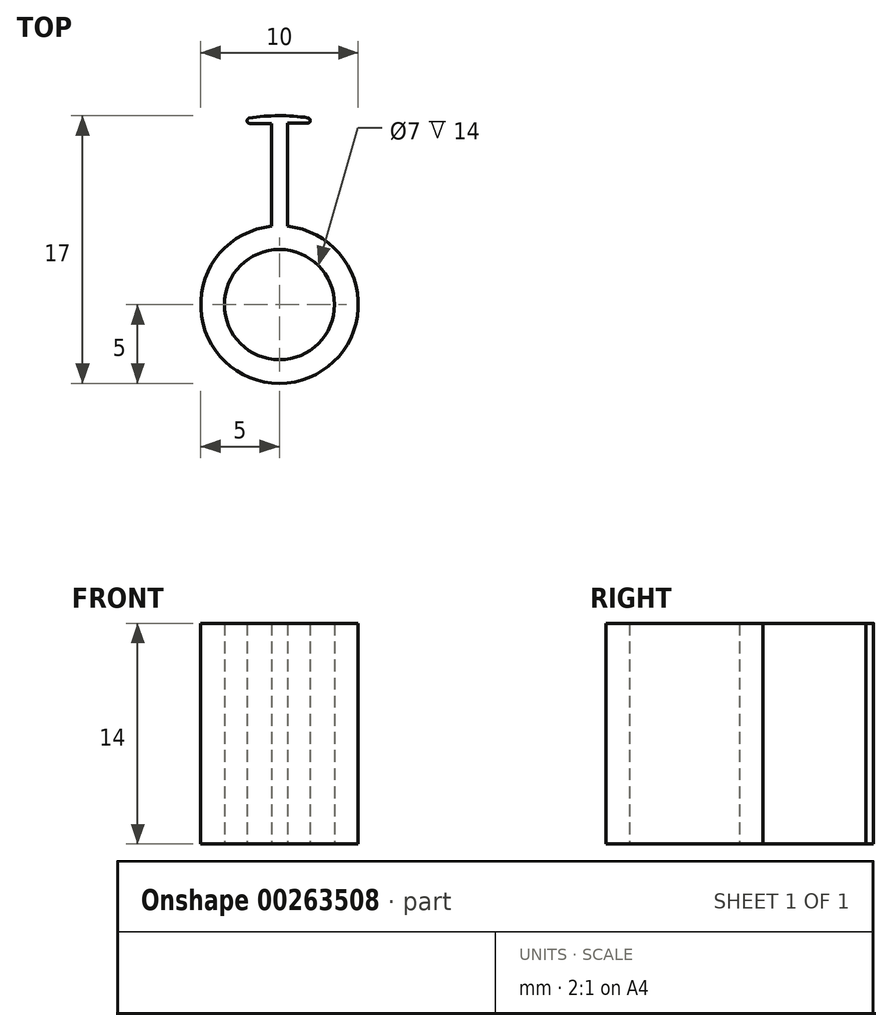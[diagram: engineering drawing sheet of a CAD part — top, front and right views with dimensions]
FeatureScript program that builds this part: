
annotation { "Feature Type Name" : "Feature", "Feature Type Description" : "" }
export const myFeature = defineFeature(function(context is Context, id is Id, definition is map)
    precondition{}
    {
        {
            var Q0;
            Q0=qCreatedBy(makeId("Top.planeOp"),FACE);
            var sketch = newSketch(context, id + "F0", { "sketchPlane" : qUnion([Q0])});
            skCircle(sketch, "E0", {"center": v(0, 0) * mm, "radius": 3.5 * mm});
            skCircle(sketch, "E1", {"center": v(0, 0) * mm, "radius": 5 * mm});
            skSolve(sketch);
        }
        {
            var Q0;
            Q0=makeQuery(id+"F0.imprint","IMPRINT",FACE,{"disambiguationData":[TD([[makeQuery(id+"F0.imprint","IMPRINT",EDGE,{"derivedFrom":sQuery(id+"F0.wireOp",EDGE,"E0")}),-1.0]])]});
            extrude(context, id + "F1", {"entities" : qUnion([Q0]), "depth" : 11 * mm});
        }
        {
            var Q0;
            Q0=makeQuery(id+"F1.opExtrude","CAP_FACE",FACE,{"disambiguationData":[OSD([sQuery(id+"F0.wireOp",EDGE,"E0"),sQuery(id+"F0.wireOp",EDGE,"E1")])],"isStart":true});
            var sketch = newSketch(context, id + "F2", { "sketchPlane" : qUnion([Q0])});
            skLineSegment(sketch, "E2.bottom", {"start": v(-0.5, 0) * mm, "end": v(0.5, 0) * mm});
            skLineSegment(sketch, "E2.top", {"start": v(-0.5, -12) * mm, "end": v(0.5, -12) * mm});
            skLineSegment(sketch, "E2.left", {"start": v(-0.5, 0) * mm, "end": v(-0.5, -12) * mm});
            skLineSegment(sketch, "E2.right", {"start": v(0.5, 0) * mm, "end": v(0.5, -12) * mm});
            skArc(sketch, "E3", {"start": v(0, -12) * mm, "mid": v(0.98, -11.96) * mm, "end": v(1.94, -11.84) * mm});
            skArc(sketch, "E4", {"start": v(0, -12) * mm, "mid": v(-1.03, -11.96) * mm, "end": v(-2.05, -11.82) * mm});
            skLineSegment(sketch, "E5", {"start": v(-2.05, -11.82) * mm, "end": v(-2.05, -11.51) * mm});
            skLineSegment(sketch, "E6", {"start": v(-2.05, -11.51) * mm, "end": v(-0.5, -11.51) * mm});
            skLineSegment(sketch, "E7", {"start": v(1.94, -11.84) * mm, "end": v(1.94, -11.53) * mm});
            skLineSegment(sketch, "E8", {"start": v(1.94, -11.53) * mm, "end": v(0.5, -11.53) * mm});
            skSolve(sketch);
        }
        {
            var Q0;
            {var subQ4=sQuery(id+"F2.wireOp",EDGE,"E5");Q0=makeQuery(id+"F2.imprint","IMPRINT",FACE,{"disambiguationData":[TD([[makeQuery(id+"F2.imprint","IMPRINT",EDGE,{"derivedFrom":subQ4}),-1.0]])]});}
            var Q1;
            {var subQ4=sQuery(id+"F2.wireOp",EDGE,"E7");Q1=makeQuery(id+"F2.imprint","IMPRINT",FACE,{"disambiguationData":[TD([[makeQuery(id+"F2.imprint","IMPRINT",EDGE,{"derivedFrom":subQ4}),1.0]])]});}
            var Q2;
            {var subQ4=sQuery(id+"F2.wireOp",EDGE,"E2.left");var subQ5=makeQuery(id+"F2.imprint","INTERSECT",VERTEX,{"derivedFrom":[subQ4,sQuery(id+"F2.wireOp",EDGE,"E6")]});Q2=makeQuery(id+"F2.imprint","IMPRINT",FACE,{"disambiguationData":[TD([[makeQuery(id+"F2.imprint","IMPRINT",EDGE,{"disambiguationData":[TD([[subQ5,1.0]])],"derivedFrom":subQ4}),1.0]])]});}
            extrude(context, id + "F3", {"entities" : qUnion([Q0, Q1, Q2]), "operationType" : NewBodyOperationType.ADD, "oppositeDirection" : true, "depth" : 11 * mm});
        }
        {
            var Q0;
            Q0=makeQuery(id+"F3.opExtrude","SWEPT_EDGE",EDGE,{"disambiguationData":[OSD([sQuery(id+"F2.wireOp",EDGE,"E5"),sQuery(id+"F2.wireOp",EDGE,"E6")])]});
            var Q1;
            Q1=makeQuery(id+"F3.opExtrude","SWEPT_EDGE",EDGE,{"disambiguationData":[OSD([sQuery(id+"F2.wireOp",EDGE,"E4"),sQuery(id+"F2.wireOp",EDGE,"E5")])]});
            var Q2;
            Q2=makeQuery(id+"F3.opExtrude","SWEPT_EDGE",EDGE,{"disambiguationData":[OSD([sQuery(id+"F2.wireOp",EDGE,"E3"),sQuery(id+"F2.wireOp",EDGE,"E7")])]});
            var Q3;
            Q3=makeQuery(id+"F3.opExtrude","SWEPT_EDGE",EDGE,{"disambiguationData":[OSD([sQuery(id+"F2.wireOp",EDGE,"E7"),sQuery(id+"F2.wireOp",EDGE,"E8")])]});
            fillet(context, id + "F4", {"entities" : qUnion([Q0, Q1, Q2, Q3]), "radius" : 0.15 * mm, "tangentPropagation" : true, "allowEdgeOverflow" : false});
        }
        {
            var Q0;
            Q0=qCreatedBy(makeId("Right.planeOp"),FACE);
            var sketch = newSketch(context, id + "F5", { "sketchPlane" : qUnion([Q0])});
            skLineSegment(sketch, "E9", {"start": v(0, 0) * mm, "end": v(0, 33.12) * mm});
            skSolve(sketch);
        }
        {
            var Q0;
            {var subQ0=sQuery(id+"F2.wireOp",EDGE,"E8");var subQ1=sQuery(id+"F2.wireOp",EDGE,"E7");var subQ2=sQuery(id+"F2.wireOp",EDGE,"E6");var subQ3=sQuery(id+"F2.wireOp",EDGE,"E5");var subQ4=sQuery(id+"F2.wireOp",EDGE,"E4");var subQ5=sQuery(id+"F2.wireOp",EDGE,"E3");var subQ6=sQuery(id+"F2.wireOp",EDGE,"E2.right");var subQ7=sQuery(id+"F2.wireOp",EDGE,"E2.left");var subQ8=sQuery(id+"F0.wireOp",EDGE,"E1");Q0=makeQuery(id+"FQCFKPcWUteTYy7_1.13.F3.boolean.opBoolean","MERGE",FACE,{"derivedFrom":[makeQuery(id+"FQCFKPcWUteTYy7_1.12.F3.boolean.opBoolean","MERGE",FACE,{"derivedFrom":[makeQuery(id+"FQCFKPcWUteTYy7_1.11.F3.boolean.opBoolean","MERGE",FACE,{"derivedFrom":[makeQuery(id+"FQCFKPcWUteTYy7_1.10.F3.boolean.opBoolean","MERGE",FACE,{"derivedFrom":[makeQuery(id+"FQCFKPcWUteTYy7_1.9.F3.boolean.opBoolean","MERGE",FACE,{"derivedFrom":[makeQuery(id+"FQCFKPcWUteTYy7_1.8.F3.boolean.opBoolean","MERGE",FACE,{"derivedFrom":[makeQuery(id+"FQCFKPcWUteTYy7_1.7.F3.boolean.opBoolean","MERGE",FACE,{"derivedFrom":[makeQuery(id+"FQCFKPcWUteTYy7_1.6.F3.boolean.opBoolean","MERGE",FACE,{"derivedFrom":[makeQuery(id+"FQCFKPcWUteTYy7_1.5.F3.boolean.opBoolean","MERGE",FACE,{"derivedFrom":[makeQuery(id+"FQCFKPcWUteTYy7_1.4.F3.boolean.opBoolean","MERGE",FACE,{"derivedFrom":[makeQuery(id+"FQCFKPcWUteTYy7_1.3.F3.boolean.opBoolean","MERGE",FACE,{"derivedFrom":[makeQuery(id+"FQCFKPcWUteTYy7_1.2.F3.boolean.opBoolean","MERGE",FACE,{"derivedFrom":[makeQuery(id+"FQCFKPcWUteTYy7_1.1.F3.boolean.opBoolean","MERGE",FACE,{"derivedFrom":[makeQuery(id+"F3.boolean.opBoolean","MERGE",FACE,{"derivedFrom":[makeQuery(id+"F1.opExtrude","CAP_FACE",FACE,{"disambiguationData":[OSD([sQuery(id+"F0.wireOp",EDGE,"E0"),subQ8])],"isStart":false}),makeQuery(id+"F3.opExtrude","CAP_FACE",FACE,{"disambiguationData":[OSD([subQ8,subQ7,subQ6,subQ5,subQ4,subQ3,subQ2,subQ1,subQ0])],"isStart":false})]}),makeQuery(id+"FQCFKPcWUteTYy7_1.1.F3.opExtrude","CAP_FACE",FACE,{"disambiguationData":[OSD([subQ8,subQ7,subQ6,subQ5,subQ4,subQ3,subQ2,subQ1,subQ0])],"isStart":false})]}),makeQuery(id+"FQCFKPcWUteTYy7_1.2.F3.opExtrude","CAP_FACE",FACE,{"disambiguationData":[OSD([subQ8,subQ7,subQ6,subQ5,subQ4,subQ3,subQ2,subQ1,subQ0])],"isStart":false})]}),makeQuery(id+"FQCFKPcWUteTYy7_1.3.F3.opExtrude","CAP_FACE",FACE,{"disambiguationData":[OSD([subQ8,subQ7,subQ6,subQ5,subQ4,subQ3,subQ2,subQ1,subQ0])],"isStart":false})]}),makeQuery(id+"FQCFKPcWUteTYy7_1.4.F3.opExtrude","CAP_FACE",FACE,{"disambiguationData":[OSD([subQ8,subQ7,subQ6,subQ5,subQ4,subQ3,subQ2,subQ1,subQ0])],"isStart":false})]}),makeQuery(id+"FQCFKPcWUteTYy7_1.5.F3.opExtrude","CAP_FACE",FACE,{"disambiguationData":[OSD([subQ8,subQ7,subQ6,subQ5,subQ4,subQ3,subQ2,subQ1,subQ0])],"isStart":false})]}),makeQuery(id+"FQCFKPcWUteTYy7_1.6.F3.opExtrude","CAP_FACE",FACE,{"disambiguationData":[OSD([subQ8,subQ7,subQ6,subQ5,subQ4,subQ3,subQ2,subQ1,subQ0])],"isStart":false})]}),makeQuery(id+"FQCFKPcWUteTYy7_1.7.F3.opExtrude","CAP_FACE",FACE,{"disambiguationData":[OSD([subQ8,subQ7,subQ6,subQ5,subQ4,subQ3,subQ2,subQ1,subQ0])],"isStart":false})]}),makeQuery(id+"FQCFKPcWUteTYy7_1.8.F3.opExtrude","CAP_FACE",FACE,{"disambiguationData":[OSD([subQ8,subQ7,subQ6,subQ5,subQ4,subQ3,subQ2,subQ1,subQ0])],"isStart":false})]}),makeQuery(id+"FQCFKPcWUteTYy7_1.9.F3.opExtrude","CAP_FACE",FACE,{"disambiguationData":[OSD([subQ8,subQ7,subQ6,subQ5,subQ4,subQ3,subQ2,subQ1,subQ0])],"isStart":false})]}),makeQuery(id+"FQCFKPcWUteTYy7_1.10.F3.opExtrude","CAP_FACE",FACE,{"disambiguationData":[OSD([subQ8,subQ7,subQ6,subQ5,subQ4,subQ3,subQ2,subQ1,subQ0])],"isStart":false})]}),makeQuery(id+"FQCFKPcWUteTYy7_1.11.F3.opExtrude","CAP_FACE",FACE,{"disambiguationData":[OSD([subQ8,subQ7,subQ6,subQ5,subQ4,subQ3,subQ2,subQ1,subQ0])],"isStart":false})]}),makeQuery(id+"FQCFKPcWUteTYy7_1.12.F3.opExtrude","CAP_FACE",FACE,{"disambiguationData":[OSD([subQ8,subQ7,subQ6,subQ5,subQ4,subQ3,subQ2,subQ1,subQ0])],"isStart":false})]}),makeQuery(id+"FQCFKPcWUteTYy7_1.13.F3.opExtrude","CAP_FACE",FACE,{"disambiguationData":[OSD([subQ8,subQ7,subQ6,subQ5,subQ4,subQ3,subQ2,subQ1,subQ0])],"isStart":false})]});}
            extrude(context, id + "F6", {"entities" : qUnion([Q0]), "operationType" : NewBodyOperationType.ADD, "depth" : 3 * mm});
        }
    });
